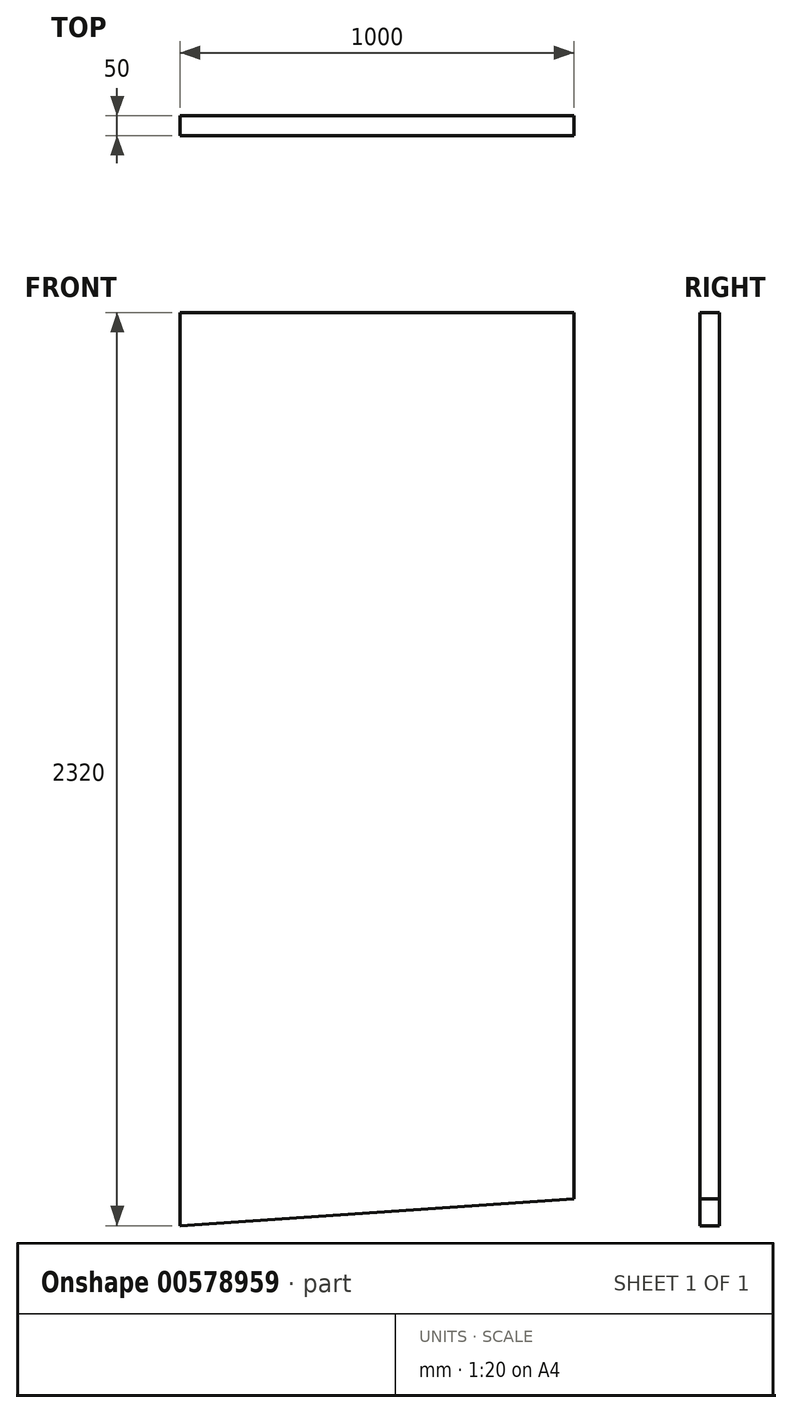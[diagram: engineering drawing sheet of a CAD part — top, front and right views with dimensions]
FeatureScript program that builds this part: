
annotation { "Feature Type Name" : "Feature", "Feature Type Description" : "" }
export const myFeature = defineFeature(function(context is Context, id is Id, definition is map)
    precondition{}
    {
        {
            var Q0;
            Q0=qCreatedBy(makeId("Front.planeOp"),FACE);
            var sketch = newSketch(context, id + "F0", { "sketchPlane" : qUnion([Q0])});
            skLineSegment(sketch, "E0.bottom", {"start": v(500, 1160) * mm, "end": v(-500, 1160) * mm});
            skLineSegment(sketch, "E0.top", {"start": v(500, -1160) * mm, "end": v(-500, -1160) * mm});
            skLineSegment(sketch, "E0.left", {"start": v(500, 1160) * mm, "end": v(500, -1160) * mm});
            skLineSegment(sketch, "E0.right", {"start": v(-500, 1160) * mm, "end": v(-500, -1160) * mm});
            skPoint(sketch, "E0.middle", {"position": v(0, 0) * mm});
            skSolve(sketch);
        }
        {
            var Q0;
            Q0=makeQuery(id+"F0.imprint","IMPRINT",FACE,{"disambiguationData":[TD([[makeQuery(id+"F0.imprint","IMPRINT",EDGE,{"derivedFrom":sQuery(id+"F0.wireOp",EDGE,"E0.bottom")}),1.0]])]});
            extrude(context, id + "F1", {"entities" : qUnion([Q0]), "endBound" : BoundingType.SYMMETRIC, "depth" : 50 * mm, "offsetDistance" : 25 * mm});
        }
        {
            var Q0;
            Q0=makeQuery(id+"F1.opExtrude","CAP_FACE",FACE,{"disambiguationData":[OSD([sQuery(id+"F0.wireOp",EDGE,"E0.bottom"),sQuery(id+"F0.wireOp",EDGE,"E0.top"),sQuery(id+"F0.wireOp",EDGE,"E0.left"),sQuery(id+"F0.wireOp",EDGE,"E0.right")])],"isStart":false});
            var sketch = newSketch(context, id + "F2", { "sketchPlane" : qUnion([Q0])});
            skLineSegment(sketch, "E1", {"start": v(-500, -1160) * mm, "end": v(500, -1091.37) * mm});
            skSolve(sketch);
        }
        {
            var Q0;
            {var subQ0=sQuery(id+"F2.wireOp",EDGE,"E1");Q0=makeQuery(id+"F2.imprint","IMPRINT",FACE,{"disambiguationData":[TD([[makeQuery(id+"F2.imprint","IMPRINT",EDGE,{"derivedFrom":subQ0}),-1.0]])]});}
            extrude(context, id + "F3", {"entities" : qUnion([Q0]), "operationType" : NewBodyOperationType.REMOVE, "oppositeDirection" : true, "depth" : 50 * mm, "offsetDistance" : 25 * mm});
        }
    });
